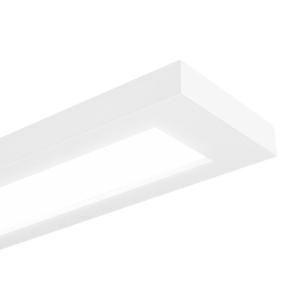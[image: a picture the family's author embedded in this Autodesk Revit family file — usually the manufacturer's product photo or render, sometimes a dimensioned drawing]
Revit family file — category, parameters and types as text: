
# Revit family: 3f_filippi_-_3f_travetta_op_3f_filippi_-_10734_-_3f_travetta_led_2x18w_op_l1290
name_source: partatom
category: Lighting Fixtures
units: mm (PartAtom-declared; Revit-internal decimal feet)

## family parameters
Cut with Voids When Loaded = No
Host = Face
Light Source = No
Part Type = Normal
Room Calculation Point = No
Round Connector Dimension = Use Diameter
Shared = No

## types (1)
- 3F Filippi - 3F Travetta OP (1 x LED, 4409 lm, 40 W, 4000 K)
    Apparent Load = 40 VA
    Approval mark = ENEC
    CIE Flux Codes = 49 81 97 100 100
    Color Rendering = 80
    Color Temperature = 4000 K
    Control Gear = Electronic ballast
    Default Elevation = 1800 mm
    Description = ILLUMINOTECHNICAL
Luminous efficiency 100% (DLOR 100%, ULOR 0%).
Initial luminous flux of the luminaire 4409 lm.
Direct symmetric distribution.
Installation Interdistance Transv.D = 1.19 x hu - Long.D = 1.20 x hu.
Tabular UGR (CIE 117 - 4H-8H; S=0.25H; 70/50/20): RUG 23.2 - 24.1.
Beam angle: 104° - 107°.
Luminous efficacy 110 lm/W.
Lifetime (L93/B10): 30000 h. (tq+25°C)
Lifetime (L90/B10): 50000 h. (tq+25°C)
Lifetime (L85/B10): 80000 h. (tq+25°C)
Lifetime (L80/B10): 100000 h. (tq+25°C)
Sudden decreased luminous flux after 50000 hours: 0% (C0).
Photobiological safety in compliance with IEC/TR 62778: RG0 risk exempt, (IEC 62471).
In compliance with IEC/EN 62722-2-1 - IEC/EN 62717 standards.

SOURCE
2 linear LED modules 18W/840.
Energy efficiency class (UE 2019/2020 - UE 2019/2015): D.
CIE 13.3 Colour rendering index: CRI >80 (R9 <50%).
IES TM-30 Fidelity Index: Rf = 84 Rg = 95.
CCT nominal colour temperature 4000 K.
Colour initial tolerance (MacAdam): SDCM 2.

MECHANICAL
Housing with squared shape in white painted galvannealed steel, with nonreflecting surface.
Flow recuperator in semi-glossy aluminium.
Opal methacrylate (PMMA) flat diffuser, anti-glare.
Luminaire with limited surface temperature. - D - (EN 60598-2-24)
Dimensions: 1290x190 mm, height 60 mm. Weight 4.365 kg.
IP20 protection degree.
Glow-wire test resistance 650°C.

ELECTRICAL
Halogen Free electronic wiring 230V-50/60Hz, power factor 0.95, THD <25%, constant output current, SELV, class I, 1 driver.
Power of the luminaire 40 W.
CE - IEC 60598-1 - EN 60598-1.
SAFE FLICKER: PstLM=<1 and SVM=<0.4 (IEC TR 61547-1 and IEC TR 63158), to ensure a more comfortable and safe light.
Luminaire compliant with EN 60598-2-22 for power supply from a centralised emergency system CPSS (Central Power Supply System), not incorporated in the luminaire - high risk areas excluded. The default power and flux are 100% in AC and 100% in DC.
Ambient temperature from 0°C to +25°C.
Temperature class T6 max 85°C.
5-pole terminal block for cascade line connection with connection capacity 2x2.5 mm².
Relative humidity UR: <85%.

INSTALLATION
Ceiling / Suspended.
All accessories dedicated to this product are available on the Catalog and on our website www.3F-Filippi.com.

APPLICATIONS
In environments, even with reduced height, requiring a comfortable light.
Exhibitions area, halls, great halls and shops.

WARNING
Luminaire designed for disposal/recycling at end-of-life.
Replaceable (LED only) light source by a professional. Replaceable control gear by a professional.
    Height = 60 mm  [stored 0.19685 ft]
    Lamp = 1 x LED
    Lamp Light Flux = 4409 lm
    Lamp Power = 40 W
    Lamp count = 1
    Length = 1290 mm
    Lifetime = 50000 h
    Luminous efficacy = 110 lm/W
    Manufacturer = 3F Filippi
    ModVariant = No
    Model = 3F Filippi - 10734 - 3F Travetta LED 2x18W OP L1290
    Mounting Place = Ceiling
    Mounting Type = Pendant
    Number of Poles = 1
    OnlyDefault = Yes
    Power Factor = 1
    Product Name = 3F Filippi - 3F Travetta OP
    Product group = pendant luminaire
    ProductGroupID = 9
    Protection Class = Protection class I
    Protection Degree = IP 20
    RLX_Detail_Level = 1
    RLX_Emergency_Light_Flux = 0 lm
    RLX_Emergency_Type = 0
    RLX_Emergency_Type_DB = No
    RlxData = <blob elided: 31421 chars, md5=b9f3a1ff>
    Socket = socket
    Standby Power = 0 W
    System Light Flux = 4409 lm
    System Power = 40 W
    Type Comments = Product without accessories
    Type Image = 3ffilippi_3f_travetta_led_op.jpg
    URL = http://relux.com
    VarID = ---
    Voltage = 0 V
    Weight = 0.00 kg
    Width = 190 mm  [stored 0.62336 ft]

note: [stored X ft] marks values corroborated as IEEE doubles in the binary element streams (Revit-internal decimal feet)

## geometry (parser evidence)
native form markers: Blend x4, Sweep x11
no freeform markers — native parametric forms only
